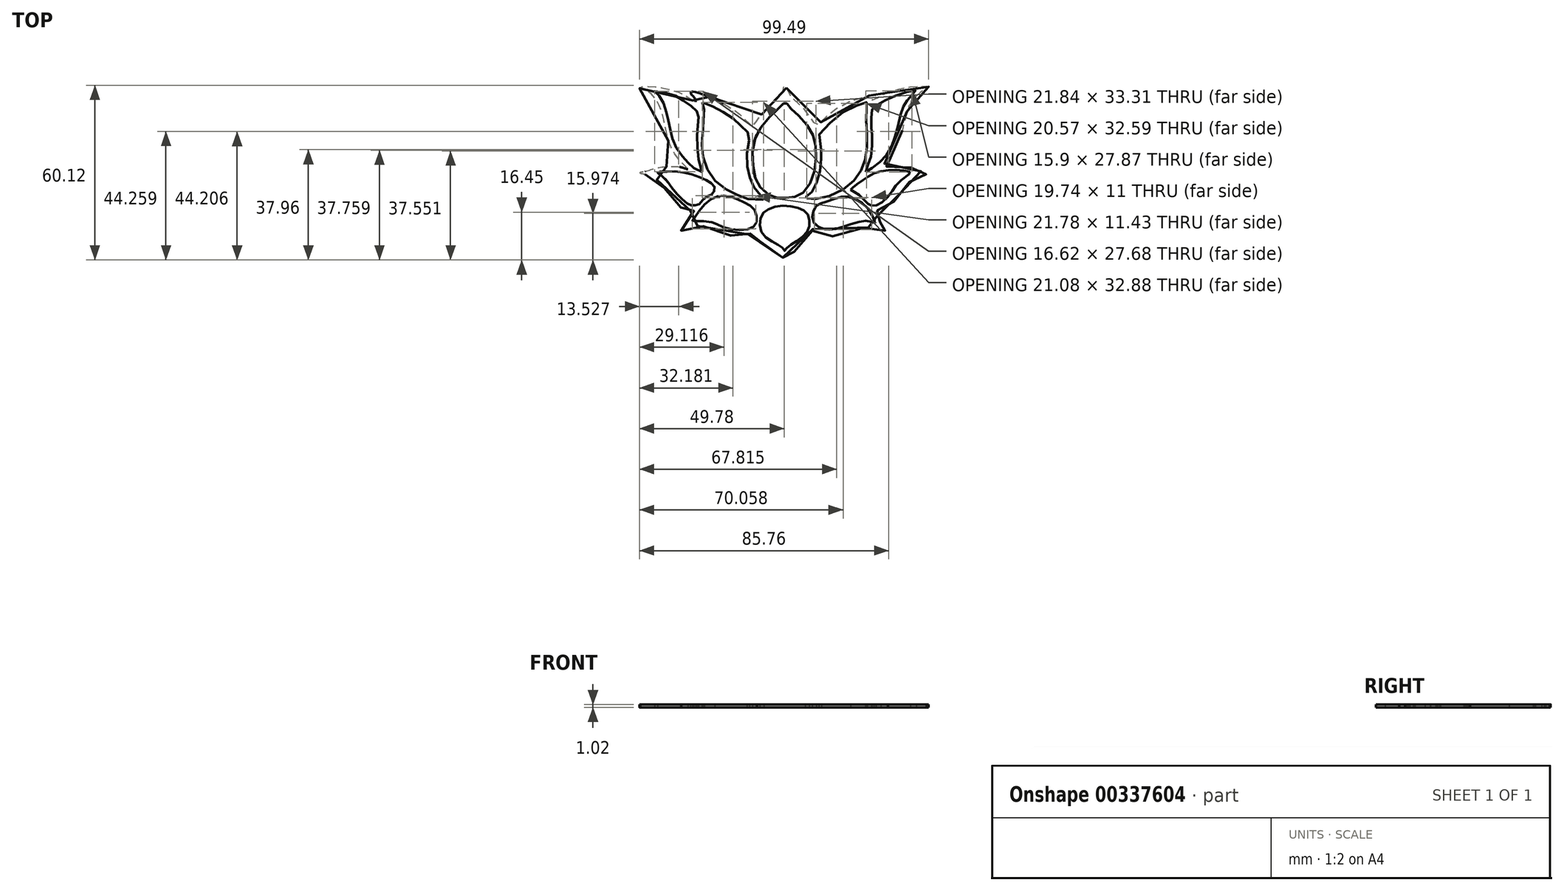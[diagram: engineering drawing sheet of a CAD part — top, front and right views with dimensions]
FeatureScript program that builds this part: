
annotation { "Feature Type Name" : "Feature", "Feature Type Description" : "" }
export const myFeature = defineFeature(function(context is Context, id is Id, definition is map)
    precondition{}
    {
        {
            var Q0;
            Q0=qCreatedBy(makeId("Top.planeOp"),FACE);
            var sketch = newSketch(context, id + "F0", { "sketchPlane" : qUnion([Q0])});
            skPoint(sketch, "E0.middle", {"position": v(0, 0) * mm});
            skFitSpline(sketch, "E1", {"points": [v(18.63, -7.04) * mm, v(21.57, -6.63) * mm, v(24.5, -5.16) * mm, v(27.44, -0.76) * mm, v(28.9, 5.95) * mm, v(28.7, 11.6) * mm, v(27.27, 15.92) * mm, v(23.72, 20.6) * mm, v(20.49, 23.51) * mm, v(19.52, 24.32) * mm, v(18.38, 26.26) * mm, v(17.74, 25.45) * mm, v(16.28, 24) * mm, v(12.4, 20.28) * mm, v(8.53, 14.62) * mm, v(7.07, 8.16) * mm, v(7.72, 1.21) * mm, v(9.17, -2.67) * mm, v(13.05, -6.06) * mm, v(15.96, -7.03) * mm, v(18.63, -7.04) * mm]});
            skPoint(sketch, "E2.119.internal.snap0", {"position": v(18, -28.41) * mm});
            skPoint(sketch, "E2.215.internal.snap0", {"position": v(18, -28.41) * mm});
            skFitSpline(sketch, "E2", {"points": [v(18.7, 30.84) * mm, v(19.15, 29.2) * mm, v(20.33, 27.73) * mm, v(23.74, 24.76) * mm, v(26.85, 20.9) * mm, v(28.78, 17.8) * mm, v(29.07, 17.46) * mm, v(29.46, 17.88) * mm, v(30.85, 19.42) * mm, v(32.47, 21.02) * mm, v(33.96, 22.36) * mm, v(36.95, 24.38) * mm, v(39.79, 25.85) * mm, v(42.77, 27) * mm, v(45.7, 27.82) * mm, v(47.72, 28.35) * mm, v(49.01, 28.64) * mm, v(49.23, 28.7) * mm, v(49.37, 28.7) * mm, v(49.5, 28.64) * mm, v(49.56, 28.48) * mm, v(49.5, 28.32) * mm, v(49.08, 27.84) * mm, v(48.63, 27.38) * mm, v(48.39, 27.06) * mm, v(48.26, 26.76) * mm, v(48.25, 26.62) * mm, v(48.28, 26.53) * mm, v(48.46, 26.63) * mm, v(49, 26.94) * mm, v(50.62, 27.86) * mm, v(53.14, 29.09) * mm, v(55.2, 29.9) * mm, v(56.94, 30.36) * mm, v(59.2, 30.86) * mm, v(61.05, 31.18) * mm, v(63.12, 31.4) * mm, v(64.6, 31.47) * mm, v(66.31, 31.43) * mm, v(67.12, 31.4) * mm, v(67.55, 31.36) * mm, v(67.65, 31.32) * mm, v(67.69, 31.22) * mm, v(67.64, 31.11) * mm, v(67.5, 31) * mm, v(67.27, 30.85) * mm, v(66.9, 30.66) * mm, v(66.34, 30.35) * mm, v(65.63, 29.92) * mm, v(64.94, 29.41) * mm, v(64.17, 28.79) * mm, v(63.5, 28.18) * mm, v(62.56, 27.16) * mm, v(61.49, 25.64) * mm, v(60.71, 24.16) * mm, v(60.15, 22.23) * mm, v(59.52, 19.97) * mm, v(58.8, 17.07) * mm, v(57.54, 12.55) * mm, v(56.58, 9.86) * mm, v(54.76, 7.17) * mm, v(52.93, 5.15) * mm, v(51.95, 4.24) * mm, v(51.26, 3.5) * mm, v(51.39, 3.46) * mm, v(52.7, 3.68) * mm, v(55.5, 3.96) * mm, v(57.96, 3.96) * mm, v(60.36, 3.65) * mm, v(61.9, 3.3) * mm, v(63.97, 2.6) * mm, v(65.82, 1.9) * mm, v(66.74, 1.58) * mm, v(66.93, 1.39) * mm, v(66.96, 1.24) * mm, v(66.74, 1.06) * mm, v(65.55, 0.87) * mm, v(63.83, 0.56) * mm, v(62.69, 0) * mm, v(61.76, -0.8) * mm, v(60.26, -2.39) * mm, v(58.63, -4.37) * mm, v(57.1, -6.44) * mm, v(55.68, -8.38) * mm, v(54.7, -9.4) * mm, v(53.54, -10.14) * mm, v(51.91, -10.87) * mm, v(50.6, -11.24) * mm, v(49.45, -11.35) * mm, v(48.98, -11.4) * mm, v(48.89, -11.47) * mm, v(48.93, -11.6) * mm, v(49.48, -12.33) * mm, v(50.36, -13.88) * mm, v(50.85, -14.98) * mm, v(51.77, -16.25) * mm, v(52.83, -17.27) * mm, v(53.23, -17.55) * mm, v(53.54, -17.96) * mm, v(53.61, -18.27) * mm, v(53.04, -18.34) * mm, v(51.86, -18) * mm, v(49.67, -17.4) * mm, v(47.94, -17.19) * mm, v(45.95, -17.26) * mm, v(43.99, -17.57) * mm, v(38.35, -19.35) * mm, v(35.1, -20.19) * mm, v(32.59, -20.3) * mm, v(29.76, -19.35) * mm, v(27.8, -17.69) * mm, v(27.67, -18.25) * mm, v(26.8, -20.61) * mm, v(24.68, -22.86) * mm, v(21.76, -25.33) * mm, v(19.93, -26.69) * mm, v(19.12, -27.37) * mm, v(18.64, -28.05) * mm, v(18.4, -28.32) * mm, v(18, -28.26) * mm, v(17.52, -27.6) * mm, v(17, -26.95) * mm, v(12.82, -24.38) * mm, v(10.64, -22.92) * mm, v(9.43, -21.55) * mm, v(8.58, -19.52) * mm, v(8.52, -17.93) * mm, v(8.12, -18.15) * mm, v(6.4, -19.24) * mm, v(5.3, -19.7) * mm, v(4.25, -20.1) * mm, v(2.6, -20.21) * mm, v(0.34, -20.07) * mm, v(-1.4, -19.73) * mm, v(-6.25, -18.13) * mm, v(-8.3, -17.18) * mm, v(-11.15, -16.64) * mm, v(-14.14, -17.32) * mm, v(-16.8, -18.4) * mm, v(-17.31, -18.54) * mm, v(-17.44, -18.23) * mm, v(-17.29, -17.92) * mm, v(-15.72, -15.54) * mm, v(-14.03, -12.85) * mm, v(-13.1, -11.51) * mm, v(-13.13, -11.41) * mm, v(-13.24, -11.43) * mm, v(-14.06, -11.49) * mm, v(-14.76, -11.47) * mm, v(-15.59, -11.3) * mm, v(-16.32, -11.08) * mm, v(-17.24, -10.54) * mm, v(-18.23, -9.6) * mm, v(-19.16, -8.7) * mm, v(-21.63, -5.8) * mm, v(-23.58, -3.23) * mm, v(-25.23, -1.23) * mm, v(-27.56, 0.39) * mm, v(-29.16, 0.96) * mm, v(-30.48, 1.21) * mm, v(-31.27, 1.36) * mm, v(-31.54, 1.57) * mm, v(-31.4, 1.86) * mm, v(-30.12, 2.07) * mm, v(-27.74, 2.82) * mm, v(-24.89, 3.53) * mm, v(-21.76, 3.84) * mm, v(-19.14, 3.8) * mm, v(-17.2, 3.5) * mm, v(-15.2, 2.89) * mm, v(-15.85, 3.65) * mm, v(-18.21, 6.22) * mm, v(-20.3, 9.15) * mm, v(-21.98, 13.19) * mm, v(-23.23, 18.78) * mm, v(-24.08, 22.48) * mm, v(-25.57, 25.9) * mm, v(-27.17, 28.3) * mm, v(-29.23, 29.8) * mm, v(-31.75, 30.7) * mm, v(-31.67, 31.12) * mm, v(-30.72, 31.3) * mm, v(-28.17, 31.4) * mm, v(-24.12, 30.91) * mm, v(-20.22, 29.99) * mm, v(-16.94, 28.8) * mm, v(-14.37, 27.17) * mm, v(-13.02, 26.17) * mm, v(-12.62, 25.82) * mm, v(-12.48, 25.75) * mm, v(-12.45, 25.87) * mm, v(-12.52, 26.37) * mm, v(-12.7, 27.08) * mm, v(-13.05, 27.71) * mm, v(-13.54, 28.18) * mm, v(-13.98, 28.67) * mm, v(-14.2, 29.12) * mm, v(-14.11, 29.44) * mm, v(-13.27, 29.53) * mm, v(-10.12, 28.69) * mm, v(-6.85, 27.47) * mm, v(-0.78, 24.17) * mm, v(3.79, 20.74) * mm, v(7.07, 17.54) * mm, v(7.07, 17.55) * mm, v(7.57, 18.22) * mm, v(9, 20.12) * mm, v(10.38, 21.9) * mm, v(12, 23.75) * mm, v(13.68, 25.38) * mm, v(15.45, 26.96) * mm, v(16.28, 27.71) * mm, v(17.2, 29.12) * mm, v(17.65, 30.18) * mm, v(17.8, 31.05) * mm, v(18, 31.62) * mm, v(18.33, 31.75) * mm, v(18.7, 30.84) * mm]});
            skFitSpline(sketch, "E3", {"points": [v(25.73, -7.1) * mm, v(27.3, -7.3) * mm, v(32.86, -6.57) * mm, v(39.56, -3.22) * mm, v(43.34, 0.76) * mm, v(45.33, 4.54) * mm, v(46.39, 9.14) * mm, v(46.5, 15.2) * mm, v(46.16, 21.03) * mm, v(46.38, 24.6) * mm, v(46.45, 25.94) * mm, v(46.08, 25.87) * mm, v(41.27, 24.09) * mm, v(34.9, 19.87) * mm, v(29.93, 14.62) * mm, v(30, 14.45) * mm, v(30.4, 11.92) * mm, v(30.71, 9.5) * mm, v(30.76, 7.16) * mm, v(30.33, 2.67) * mm, v(29.2, -1.69) * mm, v(27.44, -4.93) * mm, v(25.88, -6.33) * mm, v(25.48, -6.63) * mm, v(25.3, -6.87) * mm, v(25.33, -7.13) * mm, v(25.73, -7.1) * mm]});
            skFitSpline(sketch, "E4", {"points": [v(46, 1.92) * mm, v(47.9, 3.07) * mm, v(50.93, 5.38) * mm, v(53.55, 8.2) * mm, v(55.44, 12.09) * mm, v(56.7, 15.96) * mm, v(57.95, 21.3) * mm, v(59, 24.45) * mm, v(59.95, 26.13) * mm, v(61.94, 28.43) * mm, v(63.5, 30) * mm, v(62.58, 29.92) * mm, v(58.29, 28.96) * mm, v(53.03, 26.74) * mm, v(50.06, 25.1) * mm, v(48.43, 23.7) * mm, v(48.06, 21.7) * mm, v(47.94, 17.47) * mm, v(48.08, 15.84) * mm, v(48.23, 11.6) * mm, v(47.79, 7.02) * mm, v(46.7, 4.22) * mm, v(46, 1.92) * mm]});
            skFitSpline(sketch, "E5", {"points": [v(33.46, -17.88) * mm, v(36.32, -17.53) * mm, v(39.86, -16.4) * mm, v(43.98, -15.25) * mm, v(46.72, -14.9) * mm, v(49.46, -15.48) * mm, v(49.12, -14.9) * mm, v(47.98, -12.4) * mm, v(45.7, -9.53) * mm, v(42.15, -7.25) * mm, v(39.18, -6.56) * mm, v(36.55, -6.9) * mm, v(32.78, -8.16) * mm, v(30.5, -8.96) * mm, v(29, -9.76) * mm, v(27.98, -11.7) * mm, v(27.63, -13.53) * mm, v(28.32, -15.7) * mm, v(30.38, -17.3) * mm, v(32.43, -17.88) * mm, v(33.46, -17.88) * mm]});
            skFitSpline(sketch, "E6", {"points": [v(40.81, -4.16) * mm, v(42.06, -4.93) * mm, v(43.98, -6.18) * mm, v(46.2, -8.4) * mm, v(47.44, -9.35) * mm, v(48.6, -9.64) * mm, v(50.42, -9.26) * mm, v(53.2, -7.14) * mm, v(55.7, -3.78) * mm, v(57.53, -1.47) * mm, v(61.47, 1.8) * mm, v(61.18, 1.99) * mm, v(58.5, 2.47) * mm, v(54.36, 2.56) * mm, v(50.52, 1.99) * mm, v(47.54, 0.74) * mm, v(44.65, -1.09) * mm, v(42.16, -2.91) * mm, v(41.3, -3.68) * mm, v(40.81, -4.16) * mm]});
            skFitSpline(sketch, "E7", {"points": [v(18.14, -25.16) * mm, v(18.6, -24.59) * mm, v(19.63, -23.56) * mm, v(22.49, -21.73) * mm, v(25.23, -19.45) * mm, v(26.49, -17.27) * mm, v(26.6, -14.42) * mm, v(25.8, -12.25) * mm, v(23.74, -10.76) * mm, v(20.2, -9.85) * mm, v(15.63, -9.85) * mm, v(12.09, -11.1) * mm, v(10.37, -12.7) * mm, v(9.57, -16.02) * mm, v(10.49, -19.22) * mm, v(13.34, -21.73) * mm, v(16.32, -23.33) * mm, v(17.69, -24.47) * mm, v(18.14, -25.16) * mm]});
            skFitSpline(sketch, "E8", {"points": [v(-13.58, -14.9) * mm, v(-12.78, -15.02) * mm, v(-10.38, -14.9) * mm, v(-6.26, -15.48) * mm, v(-5.12, -16.05) * mm, v(-1.8, -17.42) * mm, v(2.77, -18) * mm, v(6.42, -17.53) * mm, v(8.14, -16.16) * mm, v(8.6, -14.1) * mm, v(8.02, -11.7) * mm, v(6.65, -9.88) * mm, v(3.9, -8.4) * mm, v(1.05, -7.02) * mm, v(-2.26, -6.22) * mm, v(-5, -6.45) * mm, v(-8.1, -8.05) * mm, v(-10.95, -11.02) * mm, v(-12.9, -13.76) * mm, v(-13.58, -14.9) * mm]});
            skFitSpline(sketch, "E9", {"points": [v(-12.66, -9.56) * mm, v(-11.4, -9.22) * mm, v(-10.03, -7.73) * mm, v(-8.2, -6.36) * mm, v(-6.83, -5.67) * mm, v(-6.03, -4.64) * mm, v(-6.03, -3.04) * mm, v(-7.29, -1.79) * mm, v(-9.69, -0.42) * mm, v(-14.37, 1.3) * mm, v(-19.63, 2.1) * mm, v(-23.74, 1.98) * mm, v(-25.57, 1.87) * mm, v(-25.23, 1.41) * mm, v(-22.71, -0.76) * mm, v(-19.97, -4.42) * mm, v(-17.11, -7.5) * mm, v(-15.06, -9.1) * mm, v(-13.68, -9.56) * mm, v(-12.66, -9.56) * mm]});
            skFitSpline(sketch, "E10", {"points": [v(-26.58, 29.75) * mm, v(-25.53, 28.7) * mm, v(-23.76, 26.11) * mm, v(-22.38, 21.83) * mm, v(-21.85, 19.22) * mm, v(-20.98, 15.36) * mm, v(-19.6, 11.12) * mm, v(-16.87, 7.13) * mm, v(-14.75, 4.77) * mm, v(-12.38, 2.9) * mm, v(-9.89, 1.9) * mm, v(-10.51, 2.77) * mm, v(-11.5, 7.13) * mm, v(-12, 13.74) * mm, v(-11.63, 18.35) * mm, v(-11.5, 21.34) * mm, v(-12.1, 22.95) * mm, v(-14.04, 24.71) * mm, v(-17.65, 27.18) * mm, v(-21.7, 28.94) * mm, v(-26.58, 29.75) * mm]});
            skFitSpline(sketch, "E11", {"points": [v(-10.16, 25.85) * mm, v(-9.83, 25.04) * mm, v(-9.51, 22.46) * mm, v(-10, 17.6) * mm, v(-10.16, 13.24) * mm, v(-10.32, 9.85) * mm, v(-9.35, 5) * mm, v(-6.6, -0.17) * mm, v(-2.24, -3.89) * mm, v(1.96, -5.99) * mm, v(5.84, -7.44) * mm, v(11.02, -7.44) * mm, v(10.7, -6.8) * mm, v(8.75, -5.02) * mm, v(6.81, -1.79) * mm, v(5.84, 1.12) * mm, v(5.2, 5.49) * mm, v(5.52, 10.98) * mm, v(6, 14.7) * mm, v(5.04, 16) * mm, v(2.93, 18.1) * mm, v(0.67, 20.2) * mm, v(-3.05, 22.62) * mm, v(-6.76, 24.56) * mm, v(-10.16, 25.85) * mm]});
            skSolve(sketch);
        }
        {
            var Q0;
            Q0=makeQuery(id+"F0.imprint","IMPRINT",FACE,{"disambiguationData":[TD([[makeQuery(id+"F0.imprint","IMPRINT",EDGE,{"derivedFrom":sQuery(id+"F0.wireOp",EDGE,"E1")}),-1.0]])]});
            extrude(context, id + "F1", {"entities" : qUnion([Q0]), "depth" : 1.02 * mm});
        }
    });
